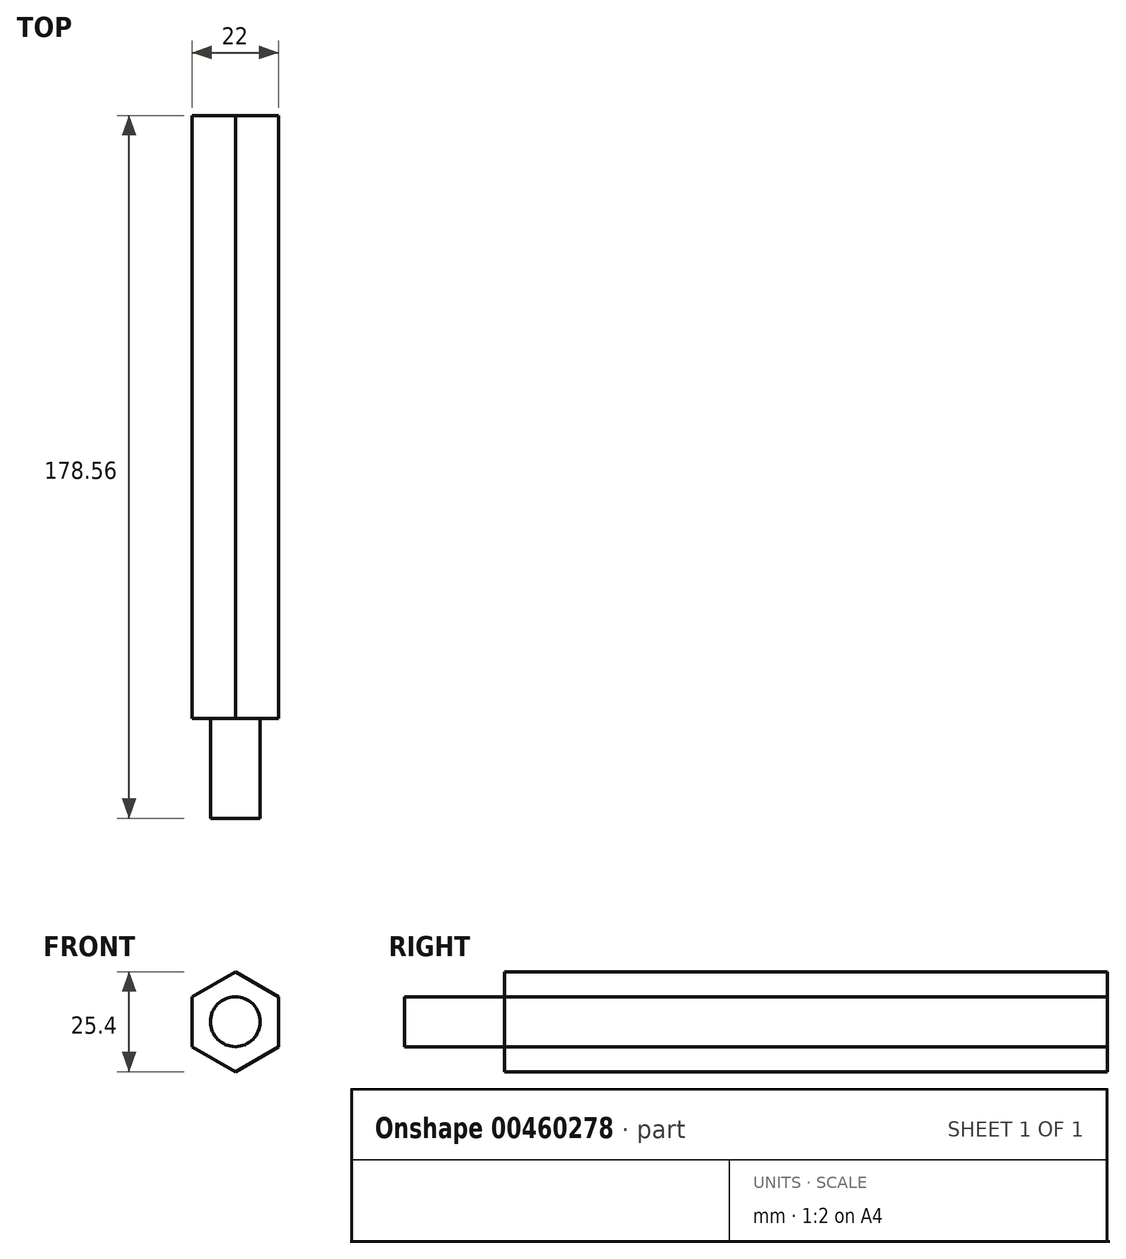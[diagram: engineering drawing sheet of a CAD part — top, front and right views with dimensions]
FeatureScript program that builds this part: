
annotation { "Feature Type Name" : "Feature", "Feature Type Description" : "" }
export const myFeature = defineFeature(function(context is Context, id is Id, definition is map)
    precondition{}
    {
        {
            var Q0;
            Q0=qCreatedBy(makeId("Front.planeOp"),FACE);
            var sketch = newSketch(context, id + "F0", { "sketchPlane" : qUnion([Q0])});
            skCircle(sketch, "E0.cCircle", {"center": v(0, 0) * mm, "radius": 12.7 * mm, "construction": true});
            skLineSegment(sketch, "E0.0", {"start": v(11, 6.35) * mm, "end": v(11, -6.35) * mm});
            skLineSegment(sketch, "E0.1", {"start": v(11, -6.35) * mm, "end": v(0, -12.7) * mm});
            skLineSegment(sketch, "E0.2", {"start": v(0, -12.7) * mm, "end": v(-11, -6.35) * mm});
            skLineSegment(sketch, "E0.3", {"start": v(-11, -6.35) * mm, "end": v(-11, 6.35) * mm});
            skLineSegment(sketch, "E0.4", {"start": v(-11, 6.35) * mm, "end": v(0, 12.7) * mm});
            skLineSegment(sketch, "E0.5", {"start": v(0, 12.7) * mm, "end": v(11, 6.35) * mm});
            skLineSegment(sketch, "E1", {"start": v(0, 12.7) * mm, "end": v(0, 0) * mm, "construction": true});
            skSolve(sketch);
        }
        {
            var Q0;
            Q0=makeQuery(id+"F0.imprint","IMPRINT",FACE,{"disambiguationData":[TD([[makeQuery(id+"F0.imprint","IMPRINT",EDGE,{"derivedFrom":sQuery(id+"F0.wireOp",EDGE,"E0.0")}),-1.0]])]});
            extrude(context, id + "F1", {"entities" : qUnion([Q0]), "depth" : 153.16 * mm});
        }
        {
            var Q0;
            Q0=makeQuery(id+"F1.opExtrude","CAP_FACE",FACE,{"disambiguationData":[OSD([sQuery(id+"F0.wireOp",EDGE,"E0.0"),sQuery(id+"F0.wireOp",EDGE,"E0.1"),sQuery(id+"F0.wireOp",EDGE,"E0.2"),sQuery(id+"F0.wireOp",EDGE,"E0.3"),sQuery(id+"F0.wireOp",EDGE,"E0.4"),sQuery(id+"F0.wireOp",EDGE,"E0.5")])],"isStart":false});
            var sketch = newSketch(context, id + "F2", { "sketchPlane" : qUnion([Q0])});
            skCircle(sketch, "E2", {"center": v(0, 0) * mm, "radius": 6.34 * mm});
            skSolve(sketch);
        }
        {
            var Q0;
            Q0=makeQuery(id+"F2.imprint","IMPRINT",FACE,{"disambiguationData":[TD([[makeQuery(id+"F2.imprint","IMPRINT",EDGE,{"derivedFrom":sQuery(id+"F2.wireOp",EDGE,"E2")}),1.0]])]});
            extrude(context, id + "F3", {"entities" : qUnion([Q0]), "operationType" : NewBodyOperationType.ADD, "depth" : 25.4 * mm});
        }
    });
